# Revit family: AFX-Cass-Linear_LED_Sconce-
name_source: partatom
category: Lighting Fixtures
units: mm (PartAtom-declared; Revit-internal decimal feet)

## family parameters
Cut with Voids When Loaded = No
Host = Face
Light Source = Yes
Part Type = Normal
Room Calculation Point = No
Round Connector Dimension = Use Diameter
Shared = No

## types (1)
- CSSS0416L30D1BK
    Apparent Load = 0 VA
    Assembly Code = D5020200
    Canopy Finish = AFX - Aluminum Black
    Color Filter = 16777215
    Colour Rendering Index = 90CRI
    Cord Finish = AFX - Plastic Black
    Default Elevation = 48"
    Description = Contemporary LED sconce with four sided illumination White acrylic diffuser - 5"W x 3 1/2"D x 16"H
    Diffuser Finish = AFX - White Acrylic
    Dimming Lamp Color Temperature Shift = <None>
    Frame Finish = AFX - Aluminum Black
    Height = 3 1/2"
    Keynote = 12500
    Length = 16"
    Manufacturer = AFX Inc
    Model = CSSS0416L30D1BK
    Photometric Web File = CSSS0416L30D1XX.IES
    Product Documentation Link = https://www.afxinc.com
    Revit File Built By = https://servex-us.com
    Tilt Angle = 0.00°
    Type Comments = Cass
    URL = https://www.afxinc.com
    Voltage = 120 V
    Wattage Comments = 18
    Width = 5"

## geometry (parser evidence)
native form markers: Sweep x1
no freeform markers — native parametric forms only
